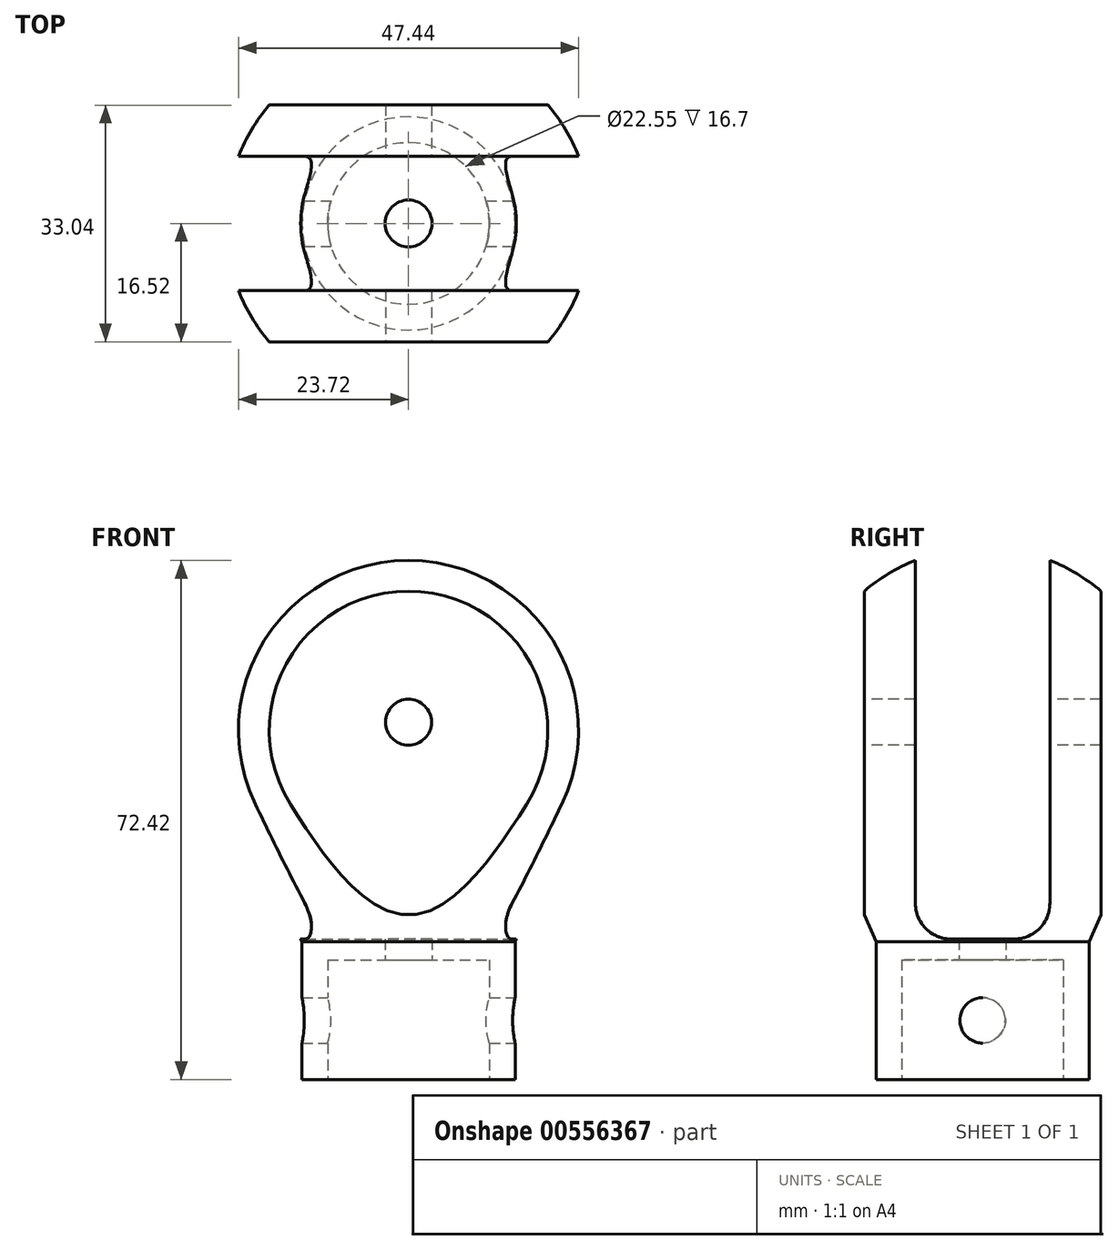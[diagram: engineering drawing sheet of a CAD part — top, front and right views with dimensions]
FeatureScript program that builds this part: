
annotation { "Feature Type Name" : "Feature", "Feature Type Description" : "" }
export const myFeature = defineFeature(function(context is Context, id is Id, definition is map)
    precondition{}
    {
        {
            var Q0;
            Q0=qCreatedBy(makeId("Front.planeOp"),FACE);
            var sketch = newSketch(context, id + "F0", { "sketchPlane" : qUnion([Q0])});
            skLineSegment(sketch, "E0.bottom", {"start": v(-14.87, -30.4) * mm, "end": v(14.75, -30.4) * mm});
            skLineSegment(sketch, "E0.top", {"start": v(-14.87, 8) * mm, "end": v(14.75, 8) * mm});
            skLineSegment(sketch, "E0.left", {"start": v(-14.87, -30.4) * mm, "end": v(-14.87, 8) * mm});
            skLineSegment(sketch, "E0.right", {"start": v(14.75, -30.4) * mm, "end": v(14.75, 8) * mm});
            skCircle(sketch, "E1", {"center": v(0, 18.3) * mm, "radius": 25.51 * mm});
            skLineSegment(sketch, "E2", {"start": v(-23.34, 8) * mm, "end": v(-14.87, -11.2) * mm});
            skLineSegment(sketch, "E3", {"start": v(23.29, 7.88) * mm, "end": v(14.75, -11.2) * mm});
            skLineSegment(sketch, "E4", {"start": v(0, 59.95) * mm, "end": v(0, -50.83) * mm, "construction": true});
            skLineSegment(sketch, "E5", {"start": v(0, 43.8) * mm, "end": v(0, -30.4) * mm});
            skSolve(sketch);
        }
        {
            var Q0;
            {var subQ4=sQuery(id+"F0.wireOp",EDGE,"E0.left");var subQ6=sQuery(id+"F0.wireOp",EDGE,"E0.top");var subQ7=makeQuery(id+"F0.imprint","INTERSECT",VERTEX,{"derivedFrom":[subQ6,subQ4]});Q0=makeQuery(id+"F0.imprint","IMPRINT",FACE,{"disambiguationData":[TD([[makeQuery(id+"F0.imprint","IMPRINT",EDGE,{"disambiguationData":[TD([[subQ7,-1.0]])],"derivedFrom":subQ6}),1.0]])]});}
            var Q1;
            {var subQ0=sQuery(id+"F0.wireOp",EDGE,"E0.left");var subQ1=sQuery(id+"F0.wireOp",EDGE,"E0.top");var subQ2=makeQuery(id+"F0.imprint","INTERSECT",VERTEX,{"derivedFrom":[subQ1,subQ0]});Q1=makeQuery(id+"F0.imprint","IMPRINT",FACE,{"disambiguationData":[TD([[makeQuery(id+"F0.imprint","IMPRINT",EDGE,{"disambiguationData":[TD([[subQ2,-1.0]])],"derivedFrom":subQ1}),-1.0]])]});}
            var Q2;
            {var subQ1=sQuery(id+"F0.wireOp",EDGE,"E0.left");var subQ5=sQuery(id+"F0.wireOp",EDGE,"E0.bottom");var subQ6=makeQuery(id+"F0.imprint","INTERSECT",VERTEX,{"derivedFrom":[subQ5,subQ1]});Q2=makeQuery(id+"F0.imprint","IMPRINT",FACE,{"disambiguationData":[TD([[makeQuery(id+"F0.imprint","IMPRINT",EDGE,{"disambiguationData":[TD([[subQ6,-1.0]])],"derivedFrom":subQ5}),1.0]])]});}
            var Q3;
            {var subQ0=sQuery(id+"F0.wireOp",EDGE,"E2");Q3=makeQuery(id+"F0.imprint","IMPRINT",FACE,{"disambiguationData":[TD([[makeQuery(id+"F0.imprint","IMPRINT",EDGE,{"derivedFrom":subQ0}),1.0]])]});}
            var Q4;
            Q4=sQuery(id+"F0.wireOp",EDGE,"E4");
            revolve(context, id + "F1", {"entities" : qUnion([Q0, Q1, Q2, Q3]), "axis" : qUnion([Q4]), "revolveType" : RevolveType.FULL});
        }
        {
            var Q0;
            Q0=qCreatedBy(makeId("Top.planeOp"),FACE);
            var sketch = newSketch(context, id + "F2", { "sketchPlane" : qUnion([Q0])});
            skLineSegment(sketch, "E6.bottom", {"start": v(-38.95, 36.12) * mm, "end": v(34.42, 36.12) * mm});
            skLineSegment(sketch, "E6.top", {"start": v(-38.95, 16.52) * mm, "end": v(34.42, 16.52) * mm});
            skLineSegment(sketch, "E6.left", {"start": v(-38.95, 36.12) * mm, "end": v(-38.95, 16.52) * mm});
            skLineSegment(sketch, "E6.right", {"start": v(34.42, 36.12) * mm, "end": v(34.42, 16.52) * mm});
            skLineSegment(sketch, "E7.MirrorCS", {"start": v(-38.95, -16.52) * mm, "end": v(34.42, -16.52) * mm});
            skLineSegment(sketch, "E8.MirrorCS", {"start": v(-38.95, -36.12) * mm, "end": v(34.42, -36.12) * mm});
            skLineSegment(sketch, "E9.MirrorCS", {"start": v(-38.95, -36.12) * mm, "end": v(-38.95, -16.52) * mm});
            skLineSegment(sketch, "E10.MirrorCS", {"start": v(34.42, -36.12) * mm, "end": v(34.42, -16.52) * mm});
            skSolve(sketch);
        }
        {
            var Q0;
            Q0 = qSketchRegion(id + "F2", true);
            extrude(context, id + "F3", {"entities" : qUnion([Q0]), "operationType" : NewBodyOperationType.REMOVE, "endBound" : BoundingType.SYMMETRIC, "depth" : 94.8 * mm, "offsetDistance" : 25 * mm});
        }
        {
            var Q0;
            Q0=qCreatedBy(makeId("Right.planeOp"),FACE);
            var sketch = newSketch(context, id + "F4", { "sketchPlane" : qUnion([Q0])});
            skLineSegment(sketch, "E11.bottom", {"start": v(9.38, 45.49) * mm, "end": v(0, 45.49) * mm});
            skLineSegment(sketch, "E11.top", {"start": v(4.38, -10.81) * mm, "end": v(0, -10.81) * mm});
            skLineSegment(sketch, "E11.left", {"start": v(9.38, 45.49) * mm, "end": v(9.38, -5.81) * mm});
            skLineSegment(sketch, "E11.right", {"start": v(0, 45.49) * mm, "end": v(0, -10.81) * mm});
            skLineSegment(sketch, "E12.MirrorCS", {"start": v(-9.38, 45.49) * mm, "end": v(0, 45.49) * mm});
            skLineSegment(sketch, "E13.MirrorCS", {"start": v(-9.38, 45.49) * mm, "end": v(-9.38, -5.81) * mm});
            skLineSegment(sketch, "E14.MirrorCS", {"start": v(-4.38, -10.81) * mm, "end": v(0, -10.81) * mm});
            skPoint(sketch, "E15.visualSharp", {"position": v(9.38, -10.81) * mm});
            skArc(sketch, "E15.filletArc", {"start": v(4.38, -10.81) * mm, "mid": v(7.92, -9.35) * mm, "end": v(9.38, -5.81) * mm});
            skPoint(sketch, "E16.visualSharp", {"position": v(-9.38, -10.81) * mm});
            skArc(sketch, "E16.filletArc", {"start": v(-9.38, -5.81) * mm, "mid": v(-7.92, -9.35) * mm, "end": v(-4.38, -10.81) * mm});
            skSolve(sketch);
        }
        {
            var Q0;
            Q0 = qSketchRegion(id + "F4", true);
            extrude(context, id + "F5", {"entities" : qUnion([Q0]), "operationType" : NewBodyOperationType.REMOVE, "endBound" : BoundingType.SYMMETRIC, "oppositeDirection" : true, "depth" : 74.2 * mm, "offsetDistance" : 25 * mm});
        }
        {
            var Q0;
            Q0=makeQuery(id+"F1.opRevolve","SWEPT_FACE",FACE,{"disambiguationData":[OSD([sQuery(id+"F0.wireOp",EDGE,"E0.bottom")])]});
            var sketch = newSketch(context, id + "F6", { "sketchPlane" : qUnion([Q0])});
            skCircle(sketch, "E17", {"center": v(0, 0) * mm, "radius": 11.28 * mm});
            skSolve(sketch);
        }
        {
            var Q0;
            Q0 = qSketchRegion(id + "F6", true);
            extrude(context, id + "F7", {"entities" : qUnion([Q0]), "operationType" : NewBodyOperationType.REMOVE, "oppositeDirection" : true, "depth" : 16.7 * mm, "offsetDistance" : 25 * mm});
        }
        {
            var Q0;
            Q0=makeQuery(id+"F3.boolean.opBoolean","COPY",FACE,{"derivedFrom":makeQuery(id+"F3.opExtrude","SWEPT_FACE",FACE,{"disambiguationData":[OSD([sQuery(id+"F2.wireOp",EDGE,"E7.MirrorCS")])]})});
            var sketch = newSketch(context, id + "F8", { "sketchPlane" : qUnion([Q0])});
            skCircle(sketch, "E18", {"center": v(0, 19.45) * mm, "radius": 3.2 * mm});
            skSolve(sketch);
        }
        {
            var Q0;
            Q0=makeQuery(id+"F8.imprint","IMPRINT",FACE,{"disambiguationData":[TD([[makeQuery(id+"F8.imprint","IMPRINT",EDGE,{"derivedFrom":sQuery(id+"F8.wireOp",EDGE,"E18")}),1.0]])]});
            var Q1;
            Q1=makeQuery(id+"F3.boolean.opBoolean","COPY",FACE,{"derivedFrom":makeQuery(id+"F3.opExtrude","SWEPT_FACE",FACE,{"disambiguationData":[OSD([sQuery(id+"F2.wireOp",EDGE,"E6.top")])]})});
            extrude(context, id + "F9", {"entities" : qUnion([Q0, Q1]), "operationType" : NewBodyOperationType.REMOVE, "oppositeDirection" : true, "depth" : 36.8 * mm, "offsetDistance" : 25 * mm});
        }
        {
            var Q0;
            Q0=makeQuery(id+"F7.boolean.opBoolean","COPY",FACE,{"derivedFrom":makeQuery(id+"F7.opExtrude","CAP_FACE",FACE,{"disambiguationData":[OSD([sQuery(id+"F6.wireOp",EDGE,"E17")])],"isStart":false})});
            var sketch = newSketch(context, id + "F10", { "sketchPlane" : qUnion([Q0])});
            skCircle(sketch, "E19", {"center": v(0, 0) * mm, "radius": 3.27 * mm});
            skSolve(sketch);
        }
        {
            var Q0;
            Q0 = qSketchRegion(id + "F10", true);
            extrude(context, id + "F11", {"entities" : qUnion([Q0]), "operationType" : NewBodyOperationType.REMOVE, "oppositeDirection" : true, "depth" : 25 * mm, "offsetDistance" : 25 * mm});
        }
        {
            var Q0;
            Q0=qCreatedBy(makeId("Right.planeOp"),FACE);
            var sketch = newSketch(context, id + "F12", { "sketchPlane" : qUnion([Q0])});
            skCircle(sketch, "E20", {"center": v(0, -22.15) * mm, "radius": 3.18 * mm});
            skSolve(sketch);
        }
        {
            var Q0;
            Q0 = qSketchRegion(id + "F12", true);
            extrude(context, id + "F13", {"entities" : qUnion([Q0]), "operationType" : NewBodyOperationType.REMOVE, "oppositeDirection" : true, "depth" : 25 * mm, "offsetDistance" : 25 * mm, "hasSecondDirection" : true, "secondDirectionOppositeDirection" : false, "secondDirectionDepth" : 25 * mm});
        }
    });
